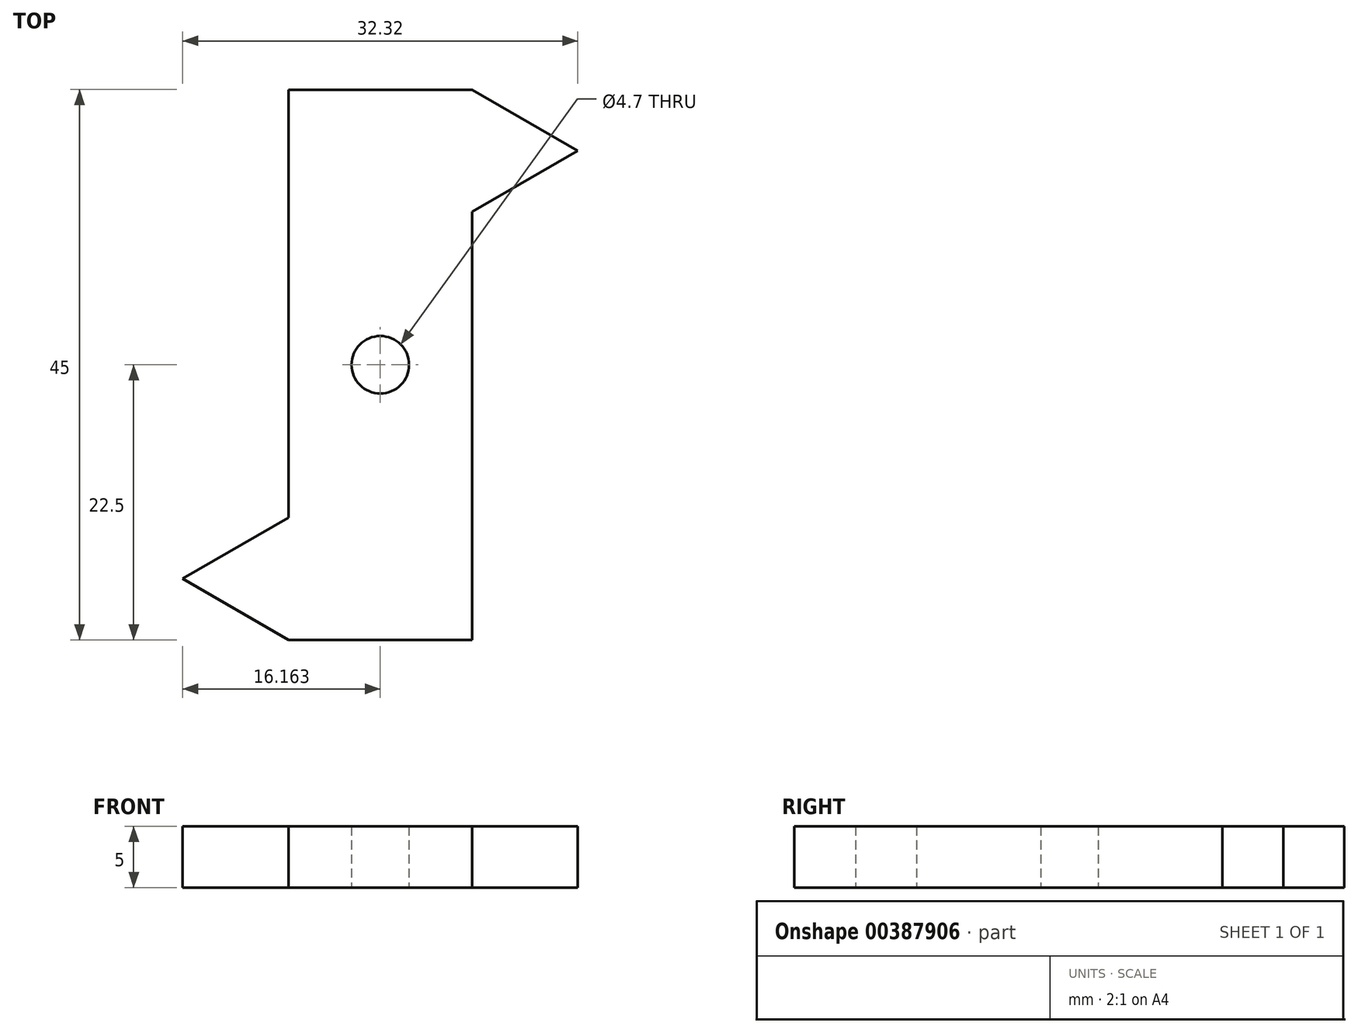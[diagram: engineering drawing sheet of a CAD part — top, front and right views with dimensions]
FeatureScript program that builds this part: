
annotation { "Feature Type Name" : "Feature", "Feature Type Description" : "" }
export const myFeature = defineFeature(function(context is Context, id is Id, definition is map)
    precondition{}
    {
        {
            var Q0;
            Q0=qCreatedBy(makeId("Top.planeOp"),FACE);
            var sketch = newSketch(context, id + "F0", { "sketchPlane" : qUnion([Q0])});
            skLineSegment(sketch, "E0.bottom", {"start": v(-39.08, -46.71) * mm, "end": v(-54.08, -46.71) * mm});
            skLineSegment(sketch, "E0.top", {"start": v(-39.08, -91.71) * mm, "end": v(-54.08, -91.71) * mm});
            skLineSegment(sketch, "E0.left", {"start": v(-39.08, -46.71) * mm, "end": v(-39.08, -91.71) * mm});
            skLineSegment(sketch, "E0.right", {"start": v(-54.08, -46.71) * mm, "end": v(-54.08, -91.71) * mm});
            skPoint(sketch, "E0.middle", {"position": v(-46.58, -69.21) * mm});
            skCircle(sketch, "E1", {"center": v(-46.58, -69.21) * mm, "radius": 2.35 * mm});
            skLineSegment(sketch, "E2", {"start": v(-39.08, -46.71) * mm, "end": v(-30.42, -51.71) * mm});
            skLineSegment(sketch, "E3", {"start": v(-30.42, -51.71) * mm, "end": v(-39.08, -51.71) * mm});
            skLineSegment(sketch, "E4.MirrorCS", {"start": v(-39.08, -56.71) * mm, "end": v(-30.42, -51.71) * mm});
            skLineSegment(sketch, "E5", {"start": v(-54.08, -91.71) * mm, "end": v(-62.74, -86.71) * mm});
            skLineSegment(sketch, "E6", {"start": v(-62.74, -86.71) * mm, "end": v(-54.08, -86.71) * mm});
            skLineSegment(sketch, "E7.MirrorCS", {"start": v(-54.08, -81.71) * mm, "end": v(-62.74, -86.71) * mm});
            skSolve(sketch);
        }
        {
            var Q0;
            {var subQ3=sQuery(id+"F0.wireOp",EDGE,"E0.bottom");Q0=makeQuery(id+"F0.imprint","IMPRINT",FACE,{"disambiguationData":[TD([[makeQuery(id+"F0.imprint","IMPRINT",EDGE,{"derivedFrom":subQ3}),1.0]])]});}
            var Q1;
            {var subQ0=sQuery(id+"F0.wireOp",EDGE,"E2");Q1=makeQuery(id+"F0.imprint","IMPRINT",FACE,{"disambiguationData":[TD([[makeQuery(id+"F0.imprint","IMPRINT",EDGE,{"derivedFrom":subQ0}),-1.0]])]});}
            var Q2;
            {var subQ0=sQuery(id+"F0.wireOp",EDGE,"E3");Q2=makeQuery(id+"F0.imprint","IMPRINT",FACE,{"disambiguationData":[TD([[makeQuery(id+"F0.imprint","IMPRINT",EDGE,{"derivedFrom":subQ0}),1.0]])]});}
            var Q3;
            {var subQ0=sQuery(id+"F0.wireOp",EDGE,"E6");Q3=makeQuery(id+"F0.imprint","IMPRINT",FACE,{"disambiguationData":[TD([[makeQuery(id+"F0.imprint","IMPRINT",EDGE,{"derivedFrom":subQ0}),1.0]])]});}
            var Q4;
            {var subQ0=sQuery(id+"F0.wireOp",EDGE,"E5");Q4=makeQuery(id+"F0.imprint","IMPRINT",FACE,{"disambiguationData":[TD([[makeQuery(id+"F0.imprint","IMPRINT",EDGE,{"derivedFrom":subQ0}),-1.0]])]});}
            extrude(context, id + "F1", {"entities" : qUnion([Q0, Q1, Q2, Q3, Q4]), "depth" : 5 * mm});
        }
    });
